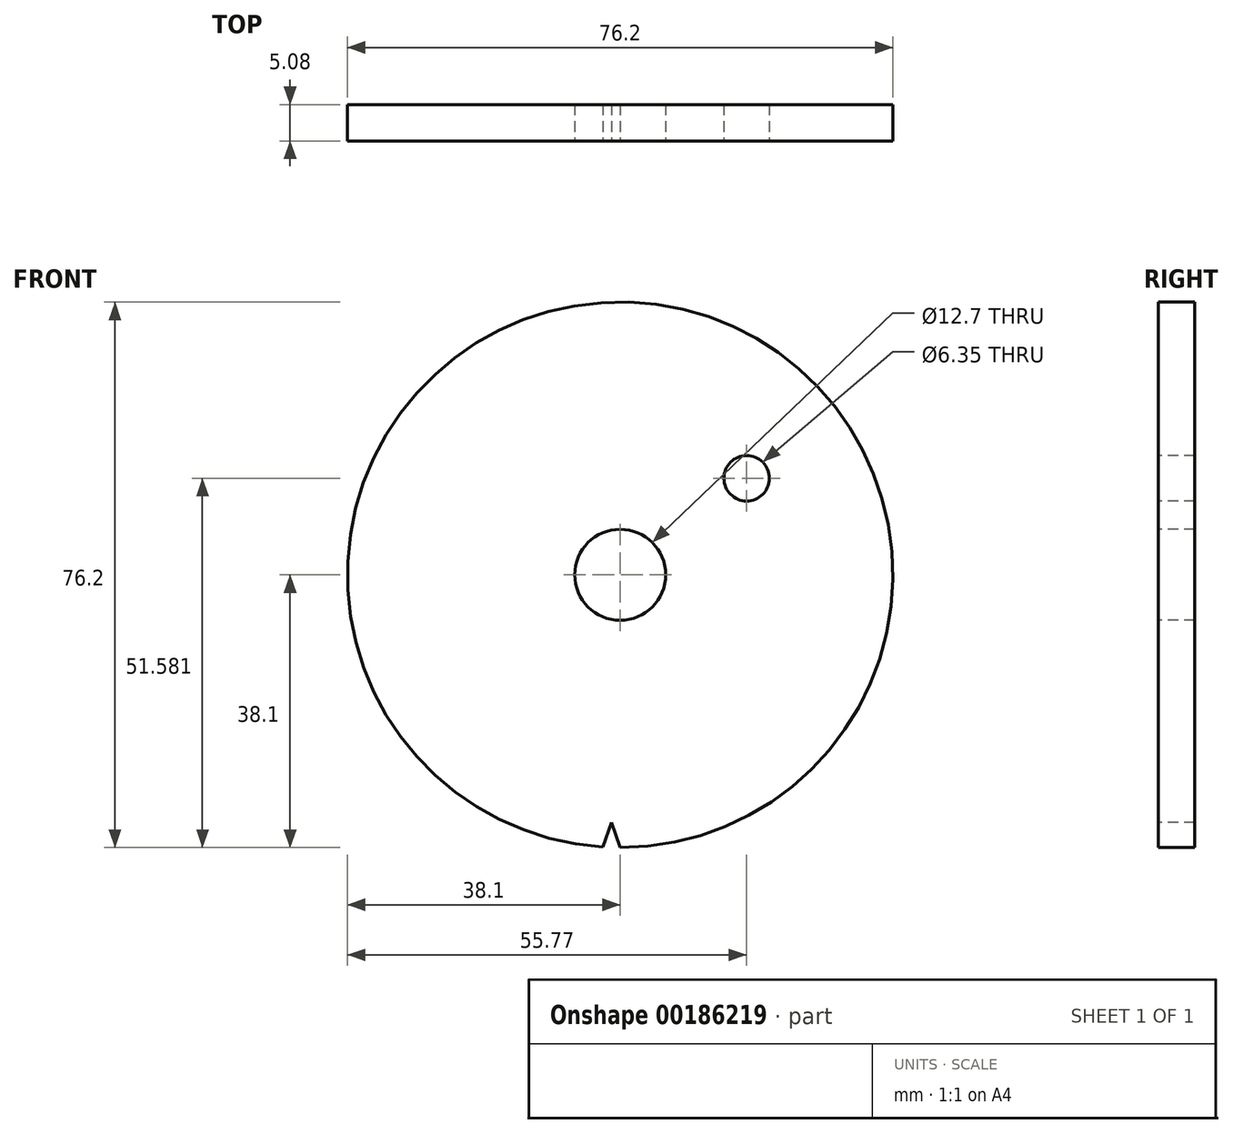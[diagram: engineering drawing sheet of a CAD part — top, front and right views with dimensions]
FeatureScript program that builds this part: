
annotation { "Feature Type Name" : "Feature", "Feature Type Description" : "" }
export const myFeature = defineFeature(function(context is Context, id is Id, definition is map)
    precondition{}
    {
        {
            var Q0;
            Q0=qCreatedBy(makeId("Front.planeOp"),FACE);
            var sketch = newSketch(context, id + "F0", { "sketchPlane" : qUnion([Q0])});
            skCircle(sketch, "E0", {"center": v(0, 0) * mm, "radius": 38.1 * mm});
            skSolve(sketch);
        }
        {
            var Q0;
            Q0=makeQuery(id+"F0.imprint","IMPRINT",FACE,{"disambiguationData":[TD([[makeQuery(id+"F0.imprint","IMPRINT",EDGE,{"derivedFrom":sQuery(id+"F0.wireOp",EDGE,"E0")}),1.0]])]});
            extrude(context, id + "F1", {"entities" : qUnion([Q0]), "depth" : 5.08 * mm});
        }
        {
            var Q0;
            Q0=qCreatedBy(makeId("Right.planeOp"),FACE);
            var sketch = newSketch(context, id + "F2", { "sketchPlane" : qUnion([Q0])});
            skLineSegment(sketch, "E1", {"start": v(0, 0) * mm, "end": v(-75.88, 0) * mm, "construction": true});
            skSolve(sketch);
        }
        {
            var Q0;
            Q0=makeQuery(id+"F1.opExtrude","CAP_FACE",FACE,{"disambiguationData":[OSD([sQuery(id+"F0.wireOp",EDGE,"E0")])],"isStart":false});
            var sketch = newSketch(context, id + "F3", { "sketchPlane" : qUnion([Q0])});
            skArc(sketch, "E2", {"start": v(-2.4, -38.02) * mm, "mid": v(-1.2, -38.08) * mm, "end": v(0, -38.1) * mm});
            skLineSegment(sketch, "E3", {"start": v(-2.4, -38.02) * mm, "end": v(-1.2, -34.63) * mm});
            skPoint(sketch, "E3.endSnap0", {"position": v(-1.2, -38.08) * mm});
            skLineSegment(sketch, "E4", {"start": v(-1.2, -34.63) * mm, "end": v(0, -38.1) * mm});
            skSolve(sketch);
        }
        {
            var Q0;
            Q0=makeQuery(id+"F3.imprint","IMPRINT",FACE,{"disambiguationData":[TD([[makeQuery(id+"F3.imprint","IMPRINT",EDGE,{"derivedFrom":sQuery(id+"F3.wireOp",EDGE,"E2")}),1.0]])]});
            extrude(context, id + "F4", {"entities" : qUnion([Q0]), "operationType" : NewBodyOperationType.REMOVE, "oppositeDirection" : true, "depth" : 25.4 * mm});
        }
        {
            var Q0;
            Q0=makeQuery(id+"F1.opExtrude","CAP_FACE",FACE,{"disambiguationData":[OSD([sQuery(id+"F0.wireOp",EDGE,"E0")])],"isStart":false});
            var sketch = newSketch(context, id + "F5", { "sketchPlane" : qUnion([Q0])});
            skCircle(sketch, "E5", {"center": v(0, 0) * mm, "radius": 6.35 * mm});
            skSolve(sketch);
        }
        {
            var Q0;
            Q0=makeQuery(id+"F5.imprint","IMPRINT",FACE,{"disambiguationData":[TD([[makeQuery(id+"F5.imprint","IMPRINT",EDGE,{"derivedFrom":sQuery(id+"F5.wireOp",EDGE,"E5")}),1.0]])]});
            extrude(context, id + "F6", {"entities" : qUnion([Q0]), "operationType" : NewBodyOperationType.REMOVE, "oppositeDirection" : true, "depth" : 25.4 * mm});
        }
        {
            var Q0;
            Q0=makeQuery(id+"F1.opExtrude","CAP_FACE",FACE,{"disambiguationData":[OSD([sQuery(id+"F0.wireOp",EDGE,"E0")])],"isStart":false});
            var sketch = newSketch(context, id + "F7", { "sketchPlane" : qUnion([Q0])});
            skCircle(sketch, "E6", {"center": v(17.67, 13.48) * mm, "radius": 3.18 * mm});
            skSolve(sketch);
        }
        {
            var Q0;
            Q0 = qSketchRegion(id + "F7", true);
            var Q1;
            Q1=sQuery(id+"F7.wireOp",EDGE,"E6");
            extrude(context, id + "F8", {"entities" : qUnion([Q0]), "operationType" : NewBodyOperationType.REMOVE, "surfaceEntities" : qUnion([Q1]), "oppositeDirection" : true, "depth" : 25.4 * mm});
        }
    });
